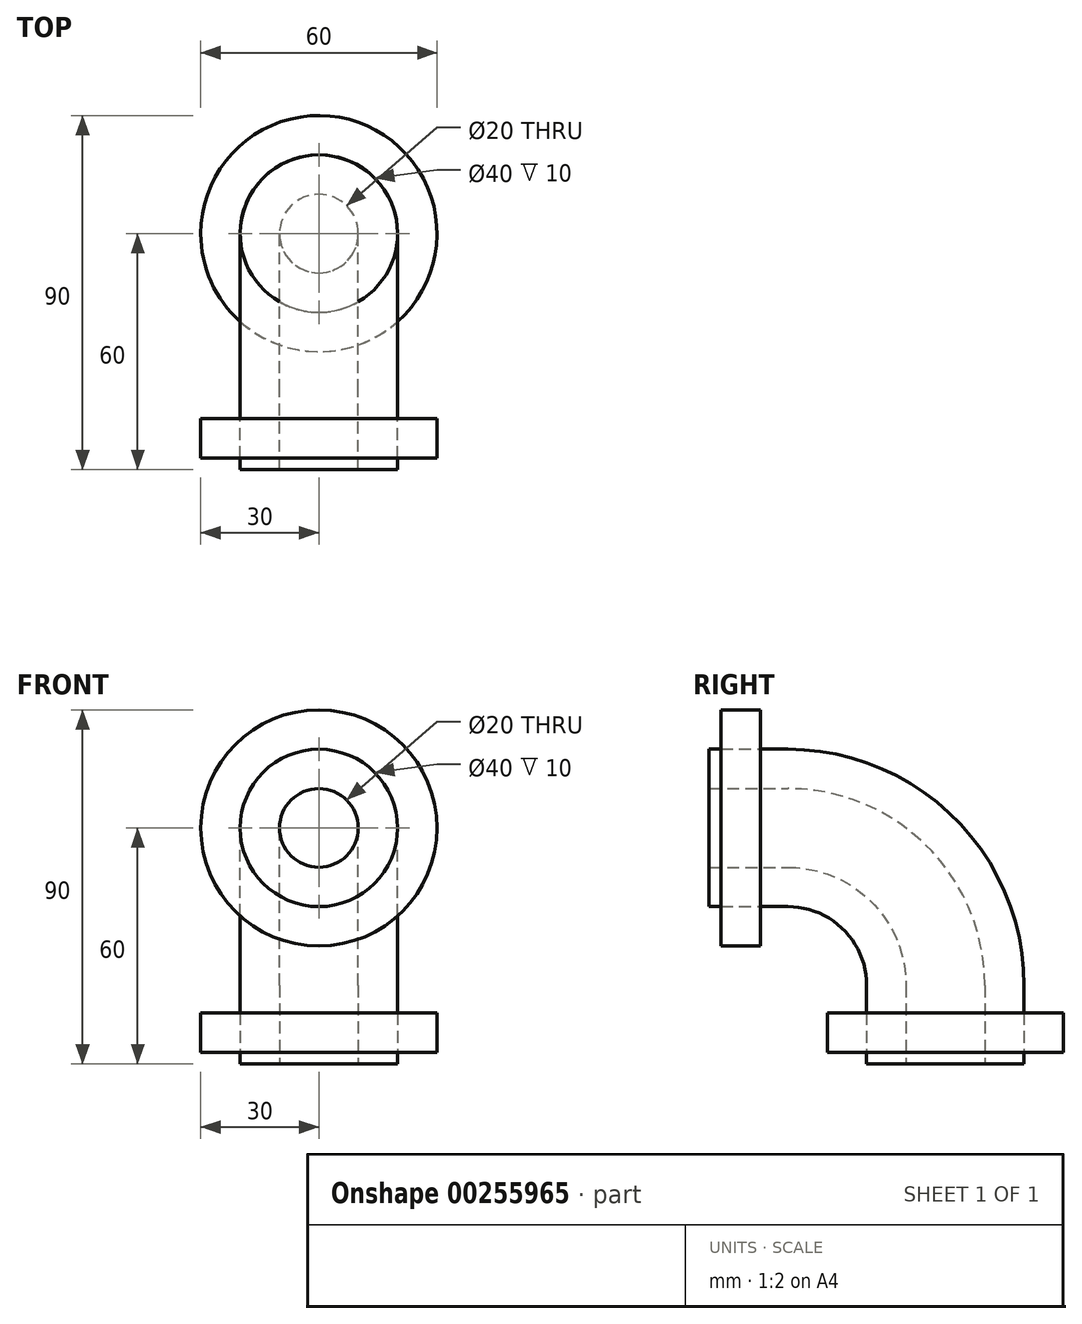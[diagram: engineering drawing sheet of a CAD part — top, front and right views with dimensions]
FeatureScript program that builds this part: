
annotation { "Feature Type Name" : "Feature", "Feature Type Description" : "" }
export const myFeature = defineFeature(function(context is Context, id is Id, definition is map)
    precondition{}
    {
        {
            var Q0;
            Q0=qCreatedBy(makeId("Front.planeOp"),FACE);
            var sketch = newSketch(context, id + "F0", { "sketchPlane" : qUnion([Q0])});
            skCircle(sketch, "E0", {"center": v(0, 0) * mm, "radius": 10 * mm});
            skCircle(sketch, "E1", {"center": v(0, 0) * mm, "radius": 20 * mm});
            skSolve(sketch);
        }
        {
            var Q0;
            Q0=qCreatedBy(makeId("Right.planeOp"),FACE);
            var sketch = newSketch(context, id + "F1", { "sketchPlane" : qUnion([Q0])});
            skLineSegment(sketch, "E2", {"start": v(0, 0) * mm, "end": v(20, 0) * mm});
            skArc(sketch, "E3", {"start": v(60, -40) * mm, "mid": v(48.28, -11.72) * mm, "end": v(20, 0) * mm});
            skLineSegment(sketch, "E4", {"start": v(60, -40) * mm, "end": v(60, -60) * mm});
            skSolve(sketch);
        }
        {
            var Q0;
            Q0=makeQuery(id+"F0.imprint","IMPRINT",FACE,{"disambiguationData":[TD([[makeQuery(id+"F0.imprint","IMPRINT",EDGE,{"derivedFrom":sQuery(id+"F0.wireOp",EDGE,"E0")}),-1.0]])]});
            var Q1;
            Q1=sQuery(id+"F1.wireOp",EDGE,"E2");
            var Q2;
            Q2=sQuery(id+"F1.wireOp",EDGE,"E3");
            var Q3;
            Q3=sQuery(id+"F1.wireOp",EDGE,"E4");
            sweep(context, id + "F2", {"profiles" : qUnion([Q0]), "path" : qUnion([Q1, Q2, Q3])});
        }
        {
            var Q0;
            Q0=makeQuery(id+"F2.opSweep","CAP_FACE",FACE,{"disambiguationData":[OSD([sQuery(id+"F0.wireOp",EDGE,"E0"),sQuery(id+"F0.wireOp",EDGE,"E1"),sQuery(id+"F1.wireOp",VERTEX,"E2.start")])],"isStart":true});
            var sketch = newSketch(context, id + "F3", { "sketchPlane" : qUnion([Q0])});
            skCircle(sketch, "E5.0.0", {"center": v(0, 0) * mm, "radius": 20 * mm});
            skCircle(sketch, "E6", {"center": v(0, 0) * mm, "radius": 30 * mm});
            skSolve(sketch);
        }
        {
            var Q0;
            Q0=makeQuery(id+"F3.imprint","IMPRINT",FACE,{"disambiguationData":[TD([[makeQuery(id+"F3.imprint","IMPRINT",EDGE,{"derivedFrom":sQuery(id+"F3.wireOp",EDGE,"E5.0.0")}),1.0]])]});
            extrude(context, id + "F4", {"entities" : qUnion([Q0]), "oppositeDirection" : true, "depth" : 13 * mm});
        }
        {
            var Q0;
            Q0=makeQuery(id+"F4.opExtrude","CAP_FACE",FACE,{"disambiguationData":[OSD([sQuery(id+"F3.wireOp",EDGE,"E5.0.0"),sQuery(id+"F3.wireOp",EDGE,"E6")])],"isStart":true});
            var sketch = newSketch(context, id + "F5", { "sketchPlane" : qUnion([Q0])});
            skSolve(sketch);
        }
        {
            var Q0;
            Q0=makeQuery(id+"F5.imprint","IMPRINT",FACE,{"disambiguationData":[TD([[makeQuery(id+"F5.imprint","IMPRINT",EDGE,{"derivedFrom":makeQuery(id+"F4.opExtrude","CAP_EDGE",EDGE,{"disambiguationData":[OSD([sQuery(id+"F3.wireOp",EDGE,"E5.0.0")])],"isStart":true})}),1.0]])]});
            extrude(context, id + "F6", {"entities" : qUnion([Q0]), "operationType" : NewBodyOperationType.REMOVE, "oppositeDirection" : true, "depth" : 3 * mm});
        }
        {
            var Q0;
            Q0=makeQuery(id+"F2.opSweep","CAP_FACE",FACE,{"disambiguationData":[OSD([sQuery(id+"F0.wireOp",EDGE,"E0"),sQuery(id+"F0.wireOp",EDGE,"E1"),sQuery(id+"F1.wireOp",VERTEX,"E4.end")])],"isStart":false});
            var sketch = newSketch(context, id + "F7", { "sketchPlane" : qUnion([Q0])});
            skCircle(sketch, "E7", {"center": v(0, -60) * mm, "radius": 30 * mm});
            skSolve(sketch);
        }
        {
            var Q0;
            Q0=makeQuery(id+"F7.imprint","IMPRINT",FACE,{"disambiguationData":[TD([[makeQuery(id+"F7.imprint","IMPRINT",EDGE,{"derivedFrom":sQuery(id+"F7.wireOp",EDGE,"E7")}),1.0]])]});
            extrude(context, id + "F8", {"entities" : qUnion([Q0]), "oppositeDirection" : true, "depth" : 13 * mm});
        }
        {
            var Q0;
            Q0=makeQuery(id+"F8.opExtrude","CAP_FACE",FACE,{"disambiguationData":[OSD([sQuery(id+"F0.wireOp",EDGE,"E1"),sQuery(id+"F1.wireOp",VERTEX,"E4.end"),sQuery(id+"F7.wireOp",EDGE,"E7")])],"isStart":true});
            extrude(context, id + "F9", {"entities" : qUnion([Q0]), "operationType" : NewBodyOperationType.REMOVE, "oppositeDirection" : true, "depth" : 3 * mm});
        }
    });
